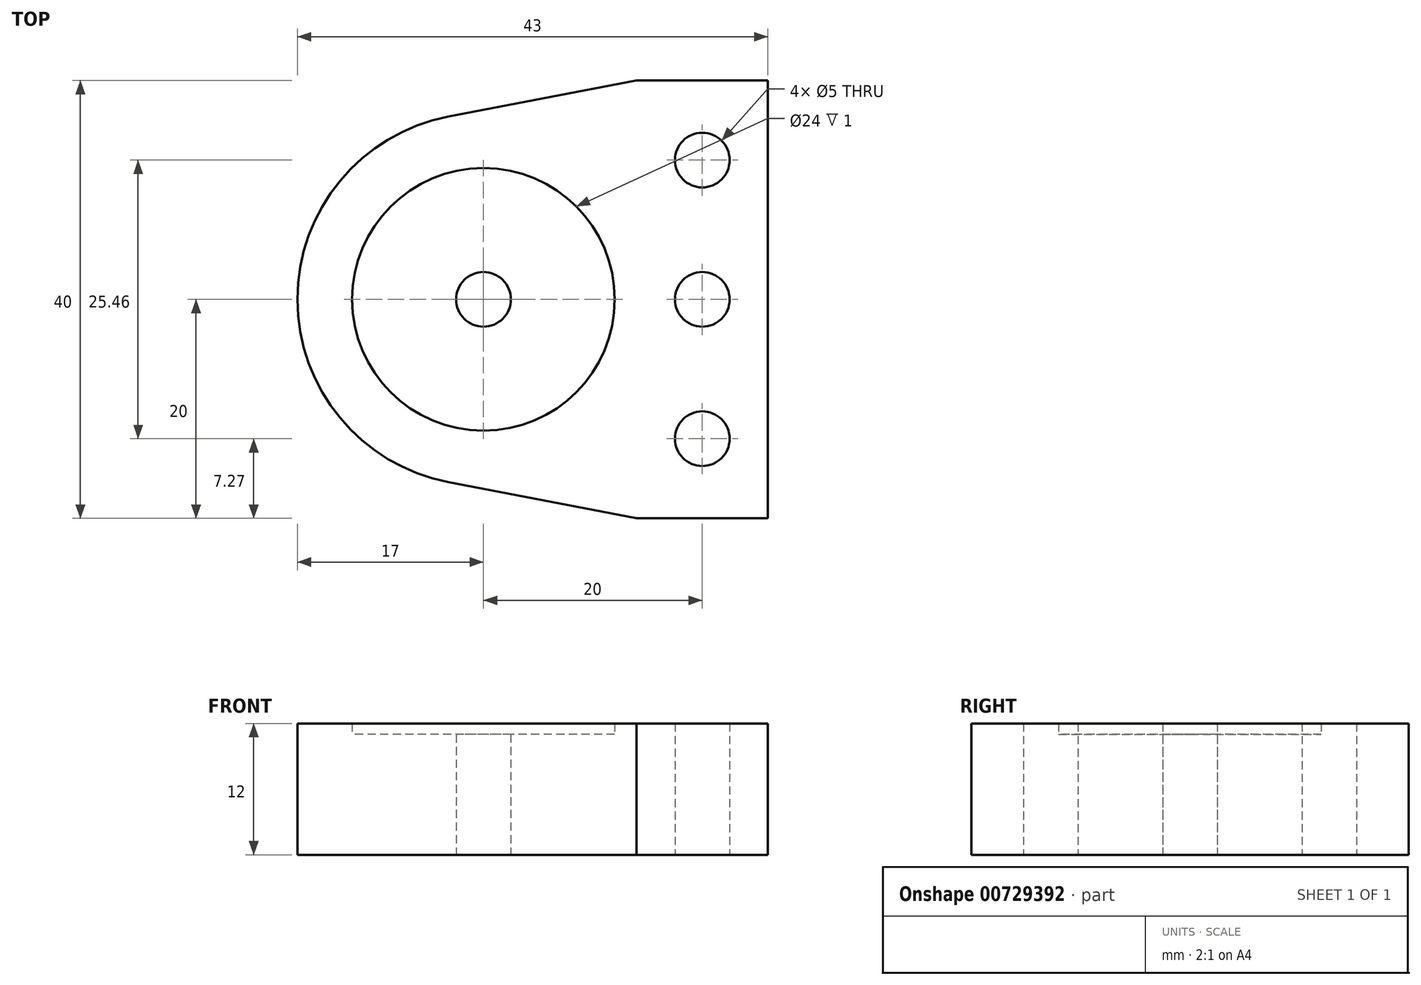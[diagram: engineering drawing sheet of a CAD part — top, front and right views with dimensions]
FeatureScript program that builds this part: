
annotation { "Feature Type Name" : "Feature", "Feature Type Description" : "" }
export const myFeature = defineFeature(function(context is Context, id is Id, definition is map)
    precondition{}
    {
        {
            var Q0;
            Q0=qCreatedBy(makeId("Top.planeOp"),FACE);
            var sketch = newSketch(context, id + "F0", { "sketchPlane" : qUnion([Q0])});
            skLineSegment(sketch, "E0.bottom", {"start": v(20, -20) * mm, "end": v(8, -20) * mm});
            skLineSegment(sketch, "E0.top", {"start": v(20, 20) * mm, "end": v(8, 20) * mm});
            skLineSegment(sketch, "E0.left", {"start": v(20, -20) * mm, "end": v(20, 20) * mm});
            skPoint(sketch, "E0.middle", {"position": v(0, 0) * mm});
            skPoint(sketch, "E1", {"position": v(14, 0) * mm});
            skPoint(sketch, "E1.positionSnap0", {"position": v(20, 0) * mm});
            skPoint(sketch, "E2", {"position": v(14, 12.73) * mm});
            skPoint(sketch, "E3", {"position": v(14, -12.73) * mm});
            skCircle(sketch, "E4", {"center": v(14, 12.73) * mm, "radius": 2.5 * mm});
            skCircle(sketch, "E5", {"center": v(14, 0) * mm, "radius": 2.5 * mm});
            skCircle(sketch, "E6", {"center": v(14, -12.73) * mm, "radius": 2.5 * mm});
            skPoint(sketch, "E7", {"position": v(8, 0) * mm});
            skPoint(sketch, "E8", {"position": v(-6, 0) * mm});
            skCircle(sketch, "E9", {"center": v(-6, 0) * mm, "radius": 12 * mm});
            skArc(sketch, "E10", {"start": v(-9.2, 16.7) * mm, "mid": v(-23, 0) * mm, "end": v(-9.2, -16.7) * mm});
            skLineSegment(sketch, "E11", {"start": v(8, -20) * mm, "end": v(8, 20) * mm});
            skLineSegment(sketch, "E12", {"start": v(8, -20) * mm, "end": v(-9.2, -16.7) * mm});
            skLineSegment(sketch, "E13", {"start": v(8, 20) * mm, "end": v(-9.2, 16.7) * mm});
            skPoint(sketch, "E14.orphan", {"position": v(-20, -20) * mm});
            skPoint(sketch, "E15.orphan", {"position": v(-20, 20) * mm});
            skPoint(sketch, "E16.trimOffspring.end.orphan", {"position": v(-20, 0) * mm});
            skCircle(sketch, "E17", {"center": v(-6, 0) * mm, "radius": 2.5 * mm});
            skSolve(sketch);
        }
        {
            var Q0;
            Q0=makeQuery(id+"F0.imprint","IMPRINT",FACE,{"disambiguationData":[TD([[makeQuery(id+"F0.imprint","IMPRINT",EDGE,{"derivedFrom":sQuery(id+"F0.wireOp",EDGE,"E0.bottom")}),-1.0]])]});
            var Q1;
            Q1=makeQuery(id+"F0.imprint","IMPRINT",FACE,{"disambiguationData":[TD([[makeQuery(id+"F0.imprint","IMPRINT",EDGE,{"derivedFrom":sQuery(id+"F0.wireOp",EDGE,"E9")}),-1.0]])]});
            extrude(context, id + "F1", {"entities" : qUnion([Q0, Q1]), "depth" : 12 * mm, "offsetDistance" : 25 * mm});
        }
        {
            var Q0;
            Q0=makeQuery(id+"F0.imprint","IMPRINT",FACE,{"disambiguationData":[TD([[makeQuery(id+"F0.imprint","IMPRINT",EDGE,{"derivedFrom":sQuery(id+"F0.wireOp",EDGE,"E9")}),1.0]])]});
            extrude(context, id + "F2", {"entities" : qUnion([Q0]), "operationType" : NewBodyOperationType.ADD, "depth" : 11 * mm, "offsetDistance" : 25 * mm});
        }
    });
